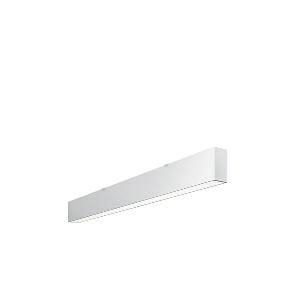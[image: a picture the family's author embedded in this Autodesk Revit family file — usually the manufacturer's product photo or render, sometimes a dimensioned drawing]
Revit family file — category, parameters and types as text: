
# Revit family: dotoo_line_-_dla_1500_840_d_end_00807930_aff3
name_source: partatom
category: Lighting Fixtures
units: mm (PartAtom-declared; Revit-internal decimal feet)

## family parameters
Cut with Voids When Loaded = No
Host = Face
Light Source = No
Part Type = Normal
Room Calculation Point = No
Round Connector Dimension = Use Diameter
Shared = No

## types (1)
- DOTOO.line - DLA 1500/840/D END (1 x LED, 1350 lm, 4000K)
    Apparent Load = 13 VA
    Approval mark = CE
    CIE Flux Codes = 67 91 98 100 100
    Color Rendering = 80-89
    Color Temperature = 4000K
    Control Gear = Electronic ballast
    Default Elevation = 1800 mm
    Description = DLA 1500/840/D|Surface-mounted luminaire.|light source: LED|work equipment: Adjustable electronic ballast, digital DALI|connected load: 220-240 V, 50/60 Hz|Power consumption: approx. 13 W|luminous flux: 1350 lm|luminous efficacy: 103 lm/W|light distribution: Direct|colour temperature: Cold white, ca. 4000 K|class of protection: I|technology: Continuously dimmable|mains lead: Connector|glare control: Prism aperture|special features: DALI Load 1x, TouchDIM - dimming via standard switch, Through-wired, up to 18 m on one mains connection, Flicker-free, Suitable as emergency lighting, Mechanical and electrical connection of the individual modules without tools|
    Frequency = 50 Hz
    Height = 110 mm
    Lamp = 1 x LED
    Lamp Light Flux = 1350 lm
    Lamp count = 1
    Length = 1128 mm
    Luminous efficacy = 104 lm/W
    Manufacturer = Waldmann
    ModVariant = No
    Model = 00807930
    Mounting Place = Ceiling
    Mounting Type = Surface mounted
    Number of Poles = 1
    OnlyDefault = Yes
    Power Factor = 1
    Product Name = DOTOO.line - DLA 1500/840/D END
    Product group = Ceiling mounted luminaire
    ProductGroupID = 3
    Protection Class = Protection class I
    Protection Degree = IP 40
    RLX_Detail_Level = 1
    RLX_Emergency_Light_Flux = 0 lm
    RLX_Emergency_Type = 0
    RLX_Emergency_Type_DB = No
    RlxData = <blob elided: 15209 chars, md5=0ee32c6e>
    Socket = socket
    Standby Power = 0 W
    System Light Flux = 1350 lm
    System Power = 13 W
    Type Comments = Product without accessories
    Type Image = 114350000-00807927.jpg
    URL = http://relux.com
    VarID = ---
    Voltage = 230 V
    Voltage Range = 220-240 V
    Weight = 0.00 kg
    Width = 60 mm  [stored 0.19685 ft]

note: [stored X ft] marks values corroborated as IEEE doubles in the binary element streams (Revit-internal decimal feet)

## geometry (parser evidence)
native form markers: Sweep x10
no freeform markers — native parametric forms only
